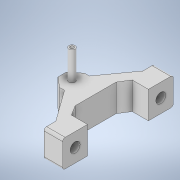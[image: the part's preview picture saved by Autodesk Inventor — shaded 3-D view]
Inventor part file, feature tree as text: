
AUTODESK INVENTOR PART (.ipt)
format: ipt  version: 2022 (Build 260153000, 153)  size: 205,312 bytes
history: native  units: mm
features: extrude x8, sketch x7, chamfer x4, hole x2, other x1, fillet x1
ambient origin geometry x8: Origin, YZ Plane, XZ Plane, XY Plane, X Axis, Y Axis, Z Axis, Center Point
bodies: Body1 (feature_tree)
feature tree (23):
  other  "Sólido1"
  extrude  "Extrusão1"  Depth=22.0mm
  hole  "Furo1"  [1 undecoded]
  extrude  "Extrusão2"  Depth=18.0mm TaperAngle=45.0deg
  chamfer  "Chanfro1"  Distance=18.0mm Angle=45.0deg
  hole  "Furo2"  [1 undecoded]
  chamfer  "Chanfro3"  Distance=10.0mm
  fillet  "Arredondamento2"  Radius=18.0mm
  extrude  "Extrusão5"  Depth=23.0mm TaperAngle=45.0deg
  chamfer  "Chanfro6"  Distance=5.0mm Angle=45.0deg
  chamfer  "Chanfro7"  Distance=3.0mm
  sketch  "Esboço12"  dims[d21=8.0mm d22=6.0mm d23=4.0mm d24=2.0mm d25=90.0deg d26=8.0mm d27=0.0mm]
  extrude  "Extrusão6"  Depth=23.0mm
  extrude  "Extrusão7"  Depth=23.0mm
  extrude  "Extrusão8"  Depth=23.0mm
  sketch  "Esboço13"  dims[d28=2.0mm d36=18.0mm d37=25.0mm d38=45.0deg d68=10.0mm d70=10.0mm d71=18.0mm d72=0.0mm d73=5.0mm d74=8.0mm d75=45.0deg d76=5.0mm d77=8.0mm d78=45.0deg d79=3.0mm d81=8.0mm d82=24.43461mm d83=24.43461mm d84=3.0mm d85=0.0mm d86=0.0mm d87=10.0mm d88=0.0mm d89=21.0mm d90=22.0mm d91=0.0mm d92=0.0mm d99=5.0mm d100=10.0mm d101=0.0mm d102=23.0mm d103=0.0mm d46=0.5mm d47=0.872665mm d48=0.5mm d49=0.872665mm d66=0.5mm d67=0.872665mm d69=0.872665mm]
  extrude  "Extrusão11"  Depth=3.0mm
  extrude  "Extrusão12"  TaperAngle=0.0deg  [1 undecoded]
  sketch  "Esboço1"  dims[d0=22.0mm d1=22.0mm]
  sketch  "Esboço2"  dims[d2=20.0mm d3=0.0mm]
  sketch  "Esboço3"  dims[d4=15.0mm d5=6.0mm d6=4.0mm d7=2.0mm d8=90.0deg d9=7.5mm d10=0.0mm d13=15.0mm]
  sketch  "Esboço4"  dims[d14=0.0mm d15=0.0mm d16=18.0mm d17=25.0mm d18=45.0deg]
  sketch  "Esboço10"  dims[d20=10.0mm]
note: 3 required parameter values undecoded (feature->parameter linkage not recoverable at this tier; creation-order binding heuristic only, values carry confidence <= 0.55)
